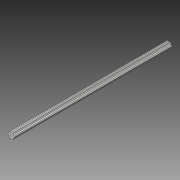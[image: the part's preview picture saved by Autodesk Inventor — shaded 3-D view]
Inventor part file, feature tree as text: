
AUTODESK INVENTOR PART (.ipt)
format: ipt  version: 2018 (Build 220112000, 112)  size: 108,032 bytes
history: native  units: in
note: dims shown in document units (in); Inventor stores cm internally (conversion verified against a paired STEP export)
features: mirror x1
ambient origin geometry x8: Origin, YZ Plane, XZ Plane, XY Plane, X Axis, Y Axis, Z Axis, Center Point
bodies: Solid1 (feature_tree)
feature tree (1):
  mirror  "Mirror1"
